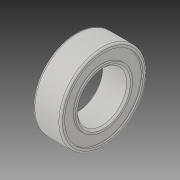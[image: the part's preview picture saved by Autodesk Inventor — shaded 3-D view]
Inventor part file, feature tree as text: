
AUTODESK INVENTOR PART (.ipt)
format: ipt  version: 2019 (Build 230136000, 136)  size: 145,920 bytes
history: native  units: in
note: dims shown in document units (in); Inventor stores cm internally (conversion verified against a paired STEP export)
features: revolve x1
ambient origin geometry x8: Origin, YZ Plane, XZ Plane, XY Plane, X Axis, Y Axis, Z Axis, Center Point
bodies: Solid1 (feature_tree)
feature tree (1):
  revolve  "Revolve1"  [1 undecoded]
note: 1 required parameter value undecoded (feature->parameter linkage not recoverable at this tier; creation-order binding heuristic only, values carry confidence <= 0.55)
